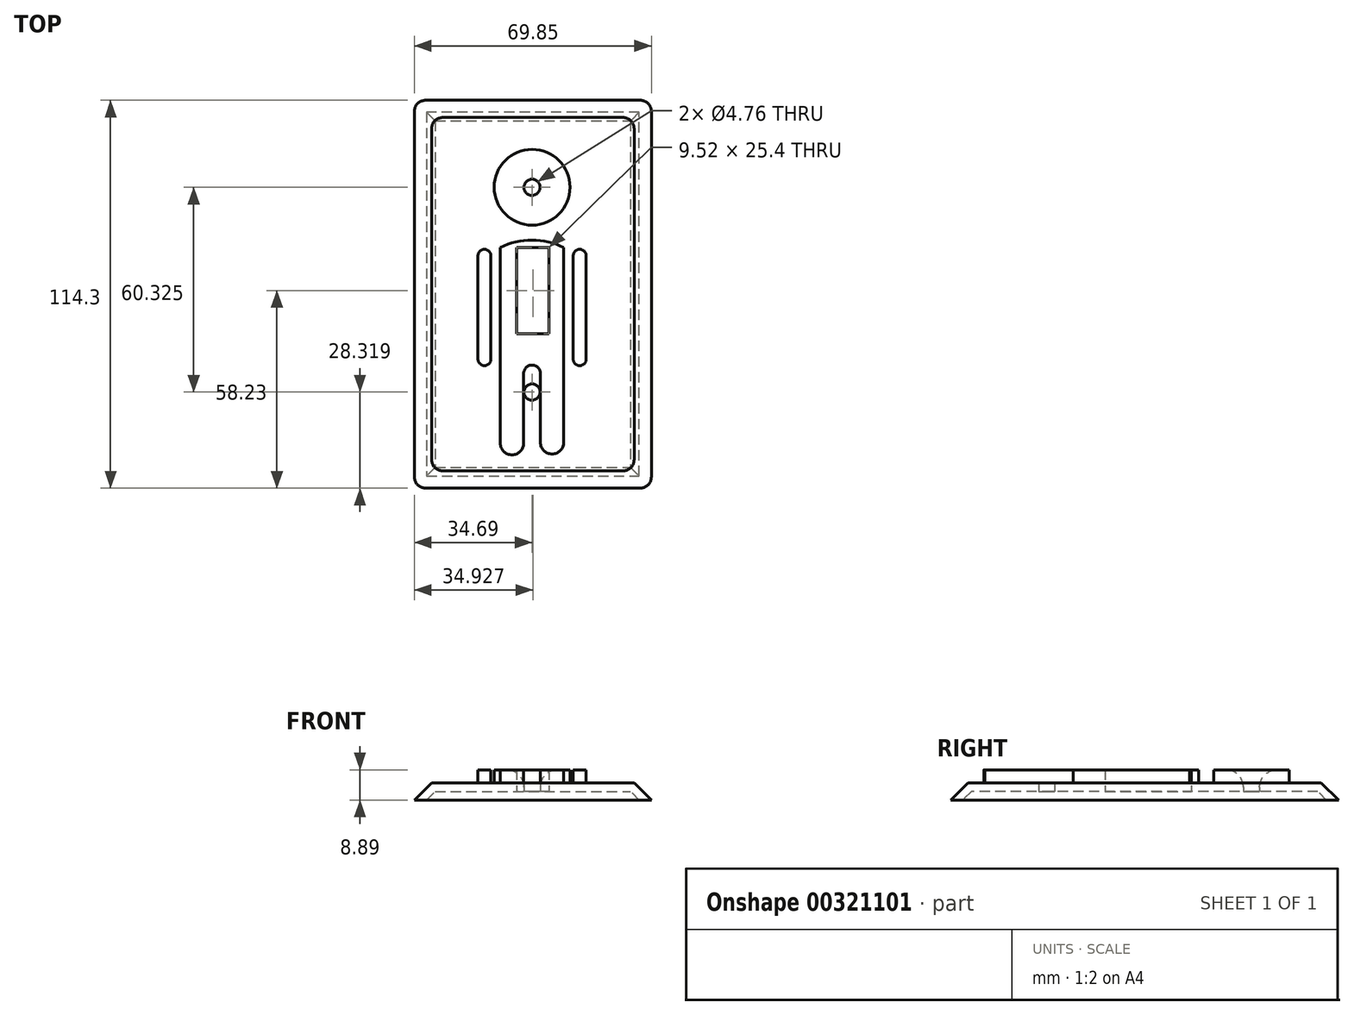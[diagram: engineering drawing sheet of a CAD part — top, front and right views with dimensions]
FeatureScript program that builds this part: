
annotation { "Feature Type Name" : "Feature", "Feature Type Description" : "" }
export const myFeature = defineFeature(function(context is Context, id is Id, definition is map)
    precondition{}
    {
        {
            var Q0;
            Q0=qCreatedBy(makeId("Top.planeOp"),FACE);
            var sketch = newSketch(context, id + "F0", { "sketchPlane" : qUnion([Q0])});
            skLineSegment(sketch, "E0.bottom", {"start": v(-34.69, 56.1) * mm, "end": v(35.16, 56.1) * mm});
            skLineSegment(sketch, "E0.top", {"start": v(-34.69, -58.2) * mm, "end": v(35.16, -58.2) * mm});
            skLineSegment(sketch, "E0.left", {"start": v(-34.69, 56.1) * mm, "end": v(-34.69, -58.2) * mm});
            skLineSegment(sketch, "E0.right", {"start": v(35.16, 56.1) * mm, "end": v(35.16, -58.2) * mm});
            skLineSegment(sketch, "E1", {"start": v(0, 56.1) * mm, "end": v(0, -58.2) * mm, "construction": true});
            skPoint(sketch, "E1.startSnap0", {"position": v(0.24, 56.1) * mm});
            skCircle(sketch, "E2", {"center": v(0, 30.44) * mm, "radius": 2.38 * mm});
            skCircle(sketch, "E3", {"center": v(0, -29.88) * mm, "radius": 2.38 * mm});
            skLineSegment(sketch, "E4.bottom", {"start": v(-4.53, 12.73) * mm, "end": v(5, 12.73) * mm});
            skLineSegment(sketch, "E4.top", {"start": v(-4.53, -12.67) * mm, "end": v(5, -12.67) * mm});
            skLineSegment(sketch, "E4.left", {"start": v(-4.53, 12.73) * mm, "end": v(-4.53, -12.67) * mm});
            skLineSegment(sketch, "E4.right", {"start": v(5, 12.73) * mm, "end": v(5, -12.67) * mm});
            skCircle(sketch, "E5", {"center": v(0, 30.44) * mm, "radius": 11.17 * mm});
            skLineSegment(sketch, "E6", {"start": v(-2.48, -44.97) * mm, "end": v(-2.48, -24.42) * mm});
            skArc(sketch, "E7", {"start": v(2.47, -24.42) * mm, "mid": v(0, -21.94) * mm, "end": v(-2.48, -24.42) * mm});
            skLineSegment(sketch, "E8", {"start": v(2.47, -24.42) * mm, "end": v(2.47, -44.73) * mm});
            skArc(sketch, "E9", {"start": v(-9.34, -44.97) * mm, "mid": v(-5.91, -48.4) * mm, "end": v(-2.48, -44.97) * mm});
            skLineSegment(sketch, "E10", {"start": v(9.33, -44.73) * mm, "end": v(9.33, -28.38) * mm});
            skLineSegment(sketch, "E11", {"start": v(-9.34, -44.97) * mm, "end": v(-9.34, -28.13) * mm});
            skLineSegment(sketch, "E12", {"start": v(-9.34, -28.13) * mm, "end": v(-9.34, 12.73) * mm});
            skLineSegment(sketch, "E13", {"start": v(9.33, 12.73) * mm, "end": v(9.33, -28.38) * mm});
            skArc(sketch, "E14", {"start": v(9.33, 12.73) * mm, "mid": v(0, 14.89) * mm, "end": v(-9.34, 12.73) * mm});
            skArc(sketch, "E15", {"start": v(2.47, -44.73) * mm, "mid": v(5.9, -48.16) * mm, "end": v(9.33, -44.73) * mm});
            skLineSegment(sketch, "E16", {"start": v(-12.13, 10.26) * mm, "end": v(-12.13, -20.22) * mm});
            skLineSegment(sketch, "E17", {"start": v(12.12, 10.26) * mm, "end": v(12.12, -20.22) * mm});
            skLineSegment(sketch, "E18", {"start": v(-15.94, 10.26) * mm, "end": v(-15.94, -20.2) * mm});
            skLineSegment(sketch, "E19", {"start": v(15.93, 10.26) * mm, "end": v(15.93, -20.22) * mm});
            skArc(sketch, "E20", {"start": v(15.93, 10.26) * mm, "mid": v(14.03, 12.16) * mm, "end": v(12.12, 10.26) * mm});
            skArc(sketch, "E21", {"start": v(12.12, -20.22) * mm, "mid": v(14.03, -22.13) * mm, "end": v(15.93, -20.22) * mm});
            skArc(sketch, "E22", {"start": v(-15.94, -20.2) * mm, "mid": v(-14.05, -22.11) * mm, "end": v(-12.13, -20.22) * mm});
            skArc(sketch, "E23", {"start": v(-12.13, 10.26) * mm, "mid": v(-14.04, 12.16) * mm, "end": v(-15.94, 10.26) * mm});
            skSolve(sketch);
        }
        {
            var Q0;
            Q0=makeQuery(id+"F0.imprint","IMPRINT",FACE,{"disambiguationData":[TD([[makeQuery(id+"F0.imprint","IMPRINT",EDGE,{"derivedFrom":sQuery(id+"F0.wireOp",EDGE,"E0.bottom")}),-1.0]])]});
            var Q1;
            Q1=makeQuery(id+"F0.imprint","IMPRINT",FACE,{"disambiguationData":[TD([[makeQuery(id+"F0.imprint","IMPRINT",EDGE,{"derivedFrom":sQuery(id+"F0.wireOp",EDGE,"E2")}),-1.0]])]});
            var Q2;
            Q2=makeQuery(id+"F0.imprint","IMPRINT",FACE,{"disambiguationData":[TD([[makeQuery(id+"F0.imprint","IMPRINT",EDGE,{"derivedFrom":sQuery(id+"F0.wireOp",EDGE,"E2")}),1.0]])]});
            var Q3;
            Q3=makeQuery(id+"F0.imprint","IMPRINT",FACE,{"disambiguationData":[TD([[makeQuery(id+"F0.imprint","IMPRINT",EDGE,{"derivedFrom":sQuery(id+"F0.wireOp",EDGE,"E4.bottom")}),1.0]])]});
            var Q4;
            Q4=makeQuery(id+"F0.imprint","IMPRINT",FACE,{"disambiguationData":[TD([[makeQuery(id+"F0.imprint","IMPRINT",EDGE,{"derivedFrom":sQuery(id+"F0.wireOp",EDGE,"E4.bottom")}),-1.0]])]});
            var Q5;
            Q5=makeQuery(id+"F0.imprint","IMPRINT",FACE,{"disambiguationData":[TD([[makeQuery(id+"F0.imprint","IMPRINT",EDGE,{"derivedFrom":sQuery(id+"F0.wireOp",EDGE,"E16")}),-1.0]])]});
            var Q6;
            Q6=makeQuery(id+"F0.imprint","IMPRINT",FACE,{"disambiguationData":[TD([[makeQuery(id+"F0.imprint","IMPRINT",EDGE,{"derivedFrom":sQuery(id+"F0.wireOp",EDGE,"E17")}),1.0]])]});
            var Q7;
            Q7=makeQuery(id+"F0.imprint","IMPRINT",FACE,{"disambiguationData":[TD([[makeQuery(id+"F0.imprint","IMPRINT",EDGE,{"derivedFrom":sQuery(id+"F0.wireOp",EDGE,"E3")}),1.0]])]});
            extrude(context, id + "F1", {"entities" : qUnion([Q0, Q1, Q2, Q3, Q4, Q5, Q6, Q7]), "depth" : 5.08 * mm});
        }
        {
            var Q0;
            Q0=makeQuery(id+"F1.opExtrude","CAP_EDGE",EDGE,{"disambiguationData":[OSD([sQuery(id+"F0.wireOp",EDGE,"E0.left")])],"isStart":false});
            var Q1;
            Q1=makeQuery(id+"F1.opExtrude","CAP_EDGE",EDGE,{"disambiguationData":[OSD([sQuery(id+"F0.wireOp",EDGE,"E0.bottom")])],"isStart":false});
            var Q2;
            Q2=makeQuery(id+"F1.opExtrude","CAP_EDGE",EDGE,{"disambiguationData":[OSD([sQuery(id+"F0.wireOp",EDGE,"E0.right")])],"isStart":false});
            var Q3;
            Q3=makeQuery(id+"F1.opExtrude","CAP_EDGE",EDGE,{"disambiguationData":[OSD([sQuery(id+"F0.wireOp",EDGE,"E0.top")])],"isStart":false});
            chamfer(context, id + "F2", {"entities" : qUnion([Q0, Q1, Q2, Q3]), "width" : 5.08 * mm, "tangentPropagation" : true});
        }
        {
            var Q0;
            Q0=makeQuery(id+"F1.opExtrude","CAP_FACE",FACE,{"disambiguationData":[OSD([sQuery(id+"F0.wireOp",EDGE,"E0.bottom"),sQuery(id+"F0.wireOp",EDGE,"E0.top"),sQuery(id+"F0.wireOp",EDGE,"E0.left"),sQuery(id+"F0.wireOp",EDGE,"E0.right")])],"isStart":true});
            shell(context, id + "F3", {"entities" : qUnion([Q0]), "thickness" : 2.54 * mm});
        }
        {
            var Q0;
            Q0=makeQuery(id+"F1.opExtrude","CAP_FACE",FACE,{"disambiguationData":[OSD([sQuery(id+"F0.wireOp",EDGE,"E0.bottom"),sQuery(id+"F0.wireOp",EDGE,"E0.top"),sQuery(id+"F0.wireOp",EDGE,"E0.left"),sQuery(id+"F0.wireOp",EDGE,"E0.right")])],"isStart":false});
            var sketch = newSketch(context, id + "F4", { "sketchPlane" : qUnion([Q0])});
            skCircle(sketch, "E24.0", {"center": v(0, 30.44) * mm, "radius": 11.17 * mm});
            skArc(sketch, "E25.0", {"start": v(9.33, 12.73) * mm, "mid": v(0, 14.89) * mm, "end": v(-9.34, 12.73) * mm});
            skLineSegment(sketch, "E26.0", {"start": v(-9.34, -28.13) * mm, "end": v(-9.34, 12.73) * mm});
            skLineSegment(sketch, "E27.0", {"start": v(-9.34, -44.97) * mm, "end": v(-9.34, -28.13) * mm});
            skArc(sketch, "E28.0", {"start": v(-9.34, -44.97) * mm, "mid": v(-5.91, -48.4) * mm, "end": v(-2.48, -44.97) * mm});
            skLineSegment(sketch, "E29.0", {"start": v(-2.48, -44.97) * mm, "end": v(-2.48, -24.42) * mm});
            skArc(sketch, "E30.0", {"start": v(2.47, -24.42) * mm, "mid": v(0, -21.94) * mm, "end": v(-2.48, -24.42) * mm});
            skLineSegment(sketch, "E31.0", {"start": v(2.47, -24.42) * mm, "end": v(2.47, -44.73) * mm});
            skArc(sketch, "E32.0", {"start": v(2.47, -44.73) * mm, "mid": v(5.9, -48.16) * mm, "end": v(9.33, -44.73) * mm});
            skLineSegment(sketch, "E33.0", {"start": v(9.33, -44.73) * mm, "end": v(9.33, -28.38) * mm});
            skLineSegment(sketch, "E34.0", {"start": v(9.33, 12.73) * mm, "end": v(9.33, -28.38) * mm});
            skLineSegment(sketch, "E35.0", {"start": v(12.12, 10.26) * mm, "end": v(12.12, -20.22) * mm});
            skLineSegment(sketch, "E36.0", {"start": v(15.93, 10.26) * mm, "end": v(15.93, -20.22) * mm});
            skArc(sketch, "E37.0", {"start": v(12.12, -20.22) * mm, "mid": v(14.03, -22.13) * mm, "end": v(15.93, -20.22) * mm});
            skArc(sketch, "E38.0", {"start": v(15.93, 10.26) * mm, "mid": v(14.03, 12.16) * mm, "end": v(12.12, 10.26) * mm});
            skArc(sketch, "E39.0", {"start": v(-12.13, 10.26) * mm, "mid": v(-14.04, 12.16) * mm, "end": v(-15.94, 10.26) * mm});
            skLineSegment(sketch, "E40.0", {"start": v(-12.13, 10.26) * mm, "end": v(-12.13, -20.22) * mm});
            skLineSegment(sketch, "E41.0", {"start": v(-15.94, 10.26) * mm, "end": v(-15.94, -20.2) * mm});
            skArc(sketch, "E42.0", {"start": v(-15.94, -20.2) * mm, "mid": v(-14.05, -22.11) * mm, "end": v(-12.13, -20.22) * mm});
            skSolve(sketch);
        }
        {
            var Q0;
            Q0 = qSketchRegion(id + "F4", true);
            extrude(context, id + "F5", {"entities" : qUnion([Q0]), "operationType" : NewBodyOperationType.ADD, "depth" : 3.8 * mm});
        }
        {
            var Q0;
            Q0=qCreatedBy(makeId("Top.planeOp"),FACE);
            var sketch = newSketch(context, id + "F6", { "sketchPlane" : qUnion([Q0])});
            skCircle(sketch, "E43.0", {"center": v(0, 30.44) * mm, "radius": 2.38 * mm});
            skLineSegment(sketch, "E44.0", {"start": v(5, 12.73) * mm, "end": v(5, -12.67) * mm});
            skLineSegment(sketch, "E45.0", {"start": v(-4.53, 12.73) * mm, "end": v(5, 12.73) * mm});
            skLineSegment(sketch, "E46.0", {"start": v(-4.53, 12.73) * mm, "end": v(-4.53, -12.67) * mm});
            skLineSegment(sketch, "E47.0", {"start": v(-4.53, -12.67) * mm, "end": v(5, -12.67) * mm});
            skCircle(sketch, "E48.0", {"center": v(0, -29.88) * mm, "radius": 2.38 * mm});
            skSolve(sketch);
        }
        {
            var Q0;
            Q0 = qSketchRegion(id + "F6", true);
            extrude(context, id + "F7", {"entities" : qUnion([Q0]), "operationType" : NewBodyOperationType.REMOVE, "endBound" : BoundingType.THROUGH_ALL, "depth" : 25.4 * mm});
        }
        {
            var Q0;
            Q0=makeQuery(id+"F2.opChamfer","BLEND_EDGE",EDGE,{"blendedFrom":[makeQuery(id+"F1.opExtrude","CAP_EDGE",EDGE,{"disambiguationData":[OSD([sQuery(id+"F0.wireOp",EDGE,"E0.bottom")])],"isStart":false}),makeQuery(id+"F1.opExtrude","CAP_EDGE",EDGE,{"disambiguationData":[OSD([sQuery(id+"F0.wireOp",EDGE,"E0.left")])],"isStart":false})],"blendedInto":[]});
            var Q1;
            Q1=makeQuery(id+"F2.opChamfer","BLEND_EDGE",EDGE,{"blendedFrom":[makeQuery(id+"F1.opExtrude","CAP_EDGE",EDGE,{"disambiguationData":[OSD([sQuery(id+"F0.wireOp",EDGE,"E0.bottom")])],"isStart":false}),makeQuery(id+"F1.opExtrude","CAP_EDGE",EDGE,{"disambiguationData":[OSD([sQuery(id+"F0.wireOp",EDGE,"E0.right")])],"isStart":false})],"blendedInto":[]});
            var Q2;
            Q2=makeQuery(id+"F2.opChamfer","BLEND_EDGE",EDGE,{"blendedFrom":[makeQuery(id+"F1.opExtrude","CAP_EDGE",EDGE,{"disambiguationData":[OSD([sQuery(id+"F0.wireOp",EDGE,"E0.top")])],"isStart":false}),makeQuery(id+"F1.opExtrude","CAP_EDGE",EDGE,{"disambiguationData":[OSD([sQuery(id+"F0.wireOp",EDGE,"E0.left")])],"isStart":false})],"blendedInto":[]});
            var Q3;
            Q3=makeQuery(id+"F2.opChamfer","BLEND_EDGE",EDGE,{"blendedFrom":[makeQuery(id+"F1.opExtrude","CAP_EDGE",EDGE,{"disambiguationData":[OSD([sQuery(id+"F0.wireOp",EDGE,"E0.top")])],"isStart":false}),makeQuery(id+"F1.opExtrude","CAP_EDGE",EDGE,{"disambiguationData":[OSD([sQuery(id+"F0.wireOp",EDGE,"E0.right")])],"isStart":false})],"blendedInto":[]});
            fillet(context, id + "F8", {"entities" : qUnion([Q0, Q1, Q2, Q3]), "radius" : 5.08 * mm, "tangentPropagation" : true, "allowEdgeOverflow" : false});
        }
        {
            var Q0;
            Q0=makeQuery(id+"F7.boolean.opBoolean","INTERSECT",EDGE,{"derivedFrom":[makeQuery(id+"F5.opExtrude","CAP_FACE",FACE,{"disambiguationData":[OSD([sQuery(id+"F4.wireOp",EDGE,"E24.0")])],"isStart":false}),makeQuery(id+"F7.opExtrude","SWEPT_FACE",FACE,{"disambiguationData":[OSD([sQuery(id+"F6.wireOp",EDGE,"E43.0")])]})]});
            fillet(context, id + "F9", {"entities" : qUnion([Q0]), "radius" : 5.08 * mm, "tangentPropagation" : true, "allowEdgeOverflow" : false});
        }
    });
